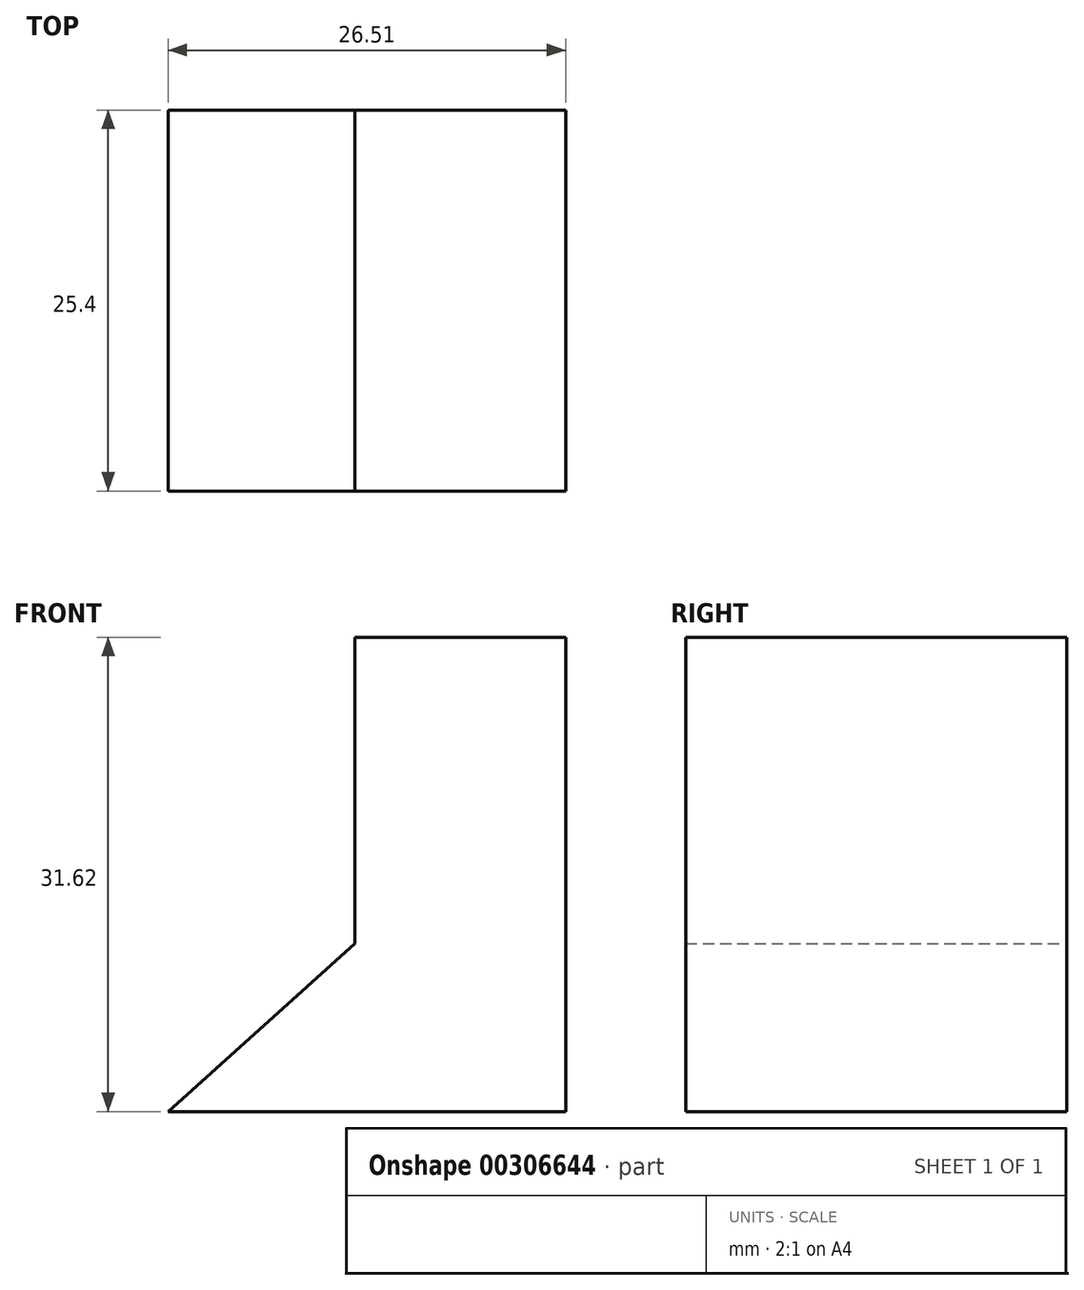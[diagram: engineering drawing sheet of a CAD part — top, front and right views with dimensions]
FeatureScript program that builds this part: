
annotation { "Feature Type Name" : "Feature", "Feature Type Description" : "" }
export const myFeature = defineFeature(function(context is Context, id is Id, definition is map)
    precondition{}
    {
        {
            var Q0;
            Q0=qCreatedBy(makeId("Front.planeOp"),FACE);
            var sketch = newSketch(context, id + "F0", { "sketchPlane" : qUnion([Q0])});
            skLineSegment(sketch, "E0", {"start": v(-50.78, 51.58) * mm, "end": v(-40.24, 51.58) * mm});
            skLineSegment(sketch, "E1", {"start": v(-40.24, 51.58) * mm, "end": v(-40.24, 19.96) * mm});
            skLineSegment(sketch, "E2", {"start": v(-40.24, 19.96) * mm, "end": v(-66.75, 19.96) * mm});
            skLineSegment(sketch, "E3", {"start": v(-66.75, 19.96) * mm, "end": v(-54.3, 31.14) * mm});
            skLineSegment(sketch, "E4", {"start": v(-54.3, 31.14) * mm, "end": v(-54.3, 51.58) * mm});
            skLineSegment(sketch, "E5", {"start": v(-50.78, 51.58) * mm, "end": v(-54.3, 51.58) * mm});
            skSolve(sketch);
        }
        {
            var Q0;
            Q0 = qSketchRegion(id + "F0", true);
            extrude(context, id + "F1", {"entities" : qUnion([Q0]), "depth" : 25.4 * mm});
        }
    });
